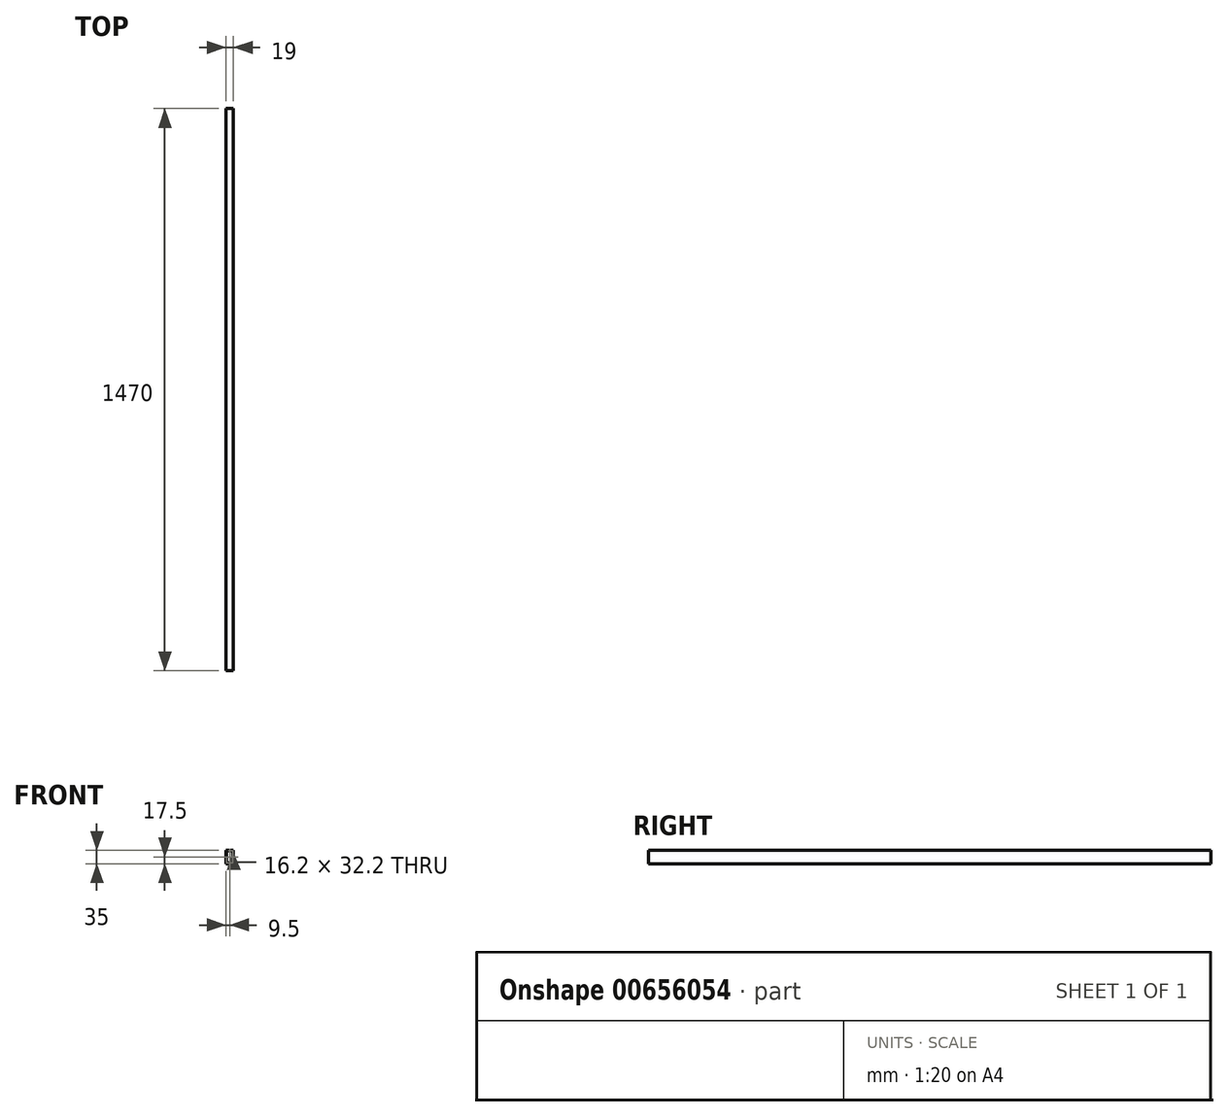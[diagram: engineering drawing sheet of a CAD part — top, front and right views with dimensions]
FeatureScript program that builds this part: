
annotation { "Feature Type Name" : "Feature", "Feature Type Description" : "" }
export const myFeature = defineFeature(function(context is Context, id is Id, definition is map)
    precondition{}
    {
        {
            var Q0;
            Q0=qCreatedBy(makeId("Front.planeOp"),FACE);
            var sketch = newSketch(context, id + "F0", { "sketchPlane" : qUnion([Q0])});
            skLineSegment(sketch, "E0.bottom", {"start": v(0, 0) * mm, "end": v(19, 0) * mm});
            skLineSegment(sketch, "E0.top", {"start": v(0, -35) * mm, "end": v(19, -35) * mm});
            skLineSegment(sketch, "E0.left", {"start": v(0, 0) * mm, "end": v(0, -35) * mm});
            skLineSegment(sketch, "E0.right", {"start": v(19, 0) * mm, "end": v(19, -35) * mm});
            skLineSegment(sketch, "E1.0", {"start": v(1.4, -1.4) * mm, "end": v(17.6, -1.4) * mm});
            skLineSegment(sketch, "E1.1", {"start": v(1.4, -1.4) * mm, "end": v(1.4, -33.6) * mm});
            skLineSegment(sketch, "E1.2", {"start": v(1.4, -33.6) * mm, "end": v(17.6, -33.6) * mm});
            skLineSegment(sketch, "E1.3", {"start": v(17.6, -1.4) * mm, "end": v(17.6, -33.6) * mm});
            skSolve(sketch);
        }
        {
            var Q0;
            Q0=makeQuery(id+"F0.imprint","IMPRINT",FACE,{"disambiguationData":[TD([[makeQuery(id+"F0.imprint","IMPRINT",EDGE,{"derivedFrom":sQuery(id+"F0.wireOp",EDGE,"E0.bottom")}),-1.0]])]});
            extrude(context, id + "F1", {"entities" : qUnion([Q0]), "depth" : 1450 * mm + 20 * mm, "offsetDistance" : 25.4 * mm});
        }
    });
